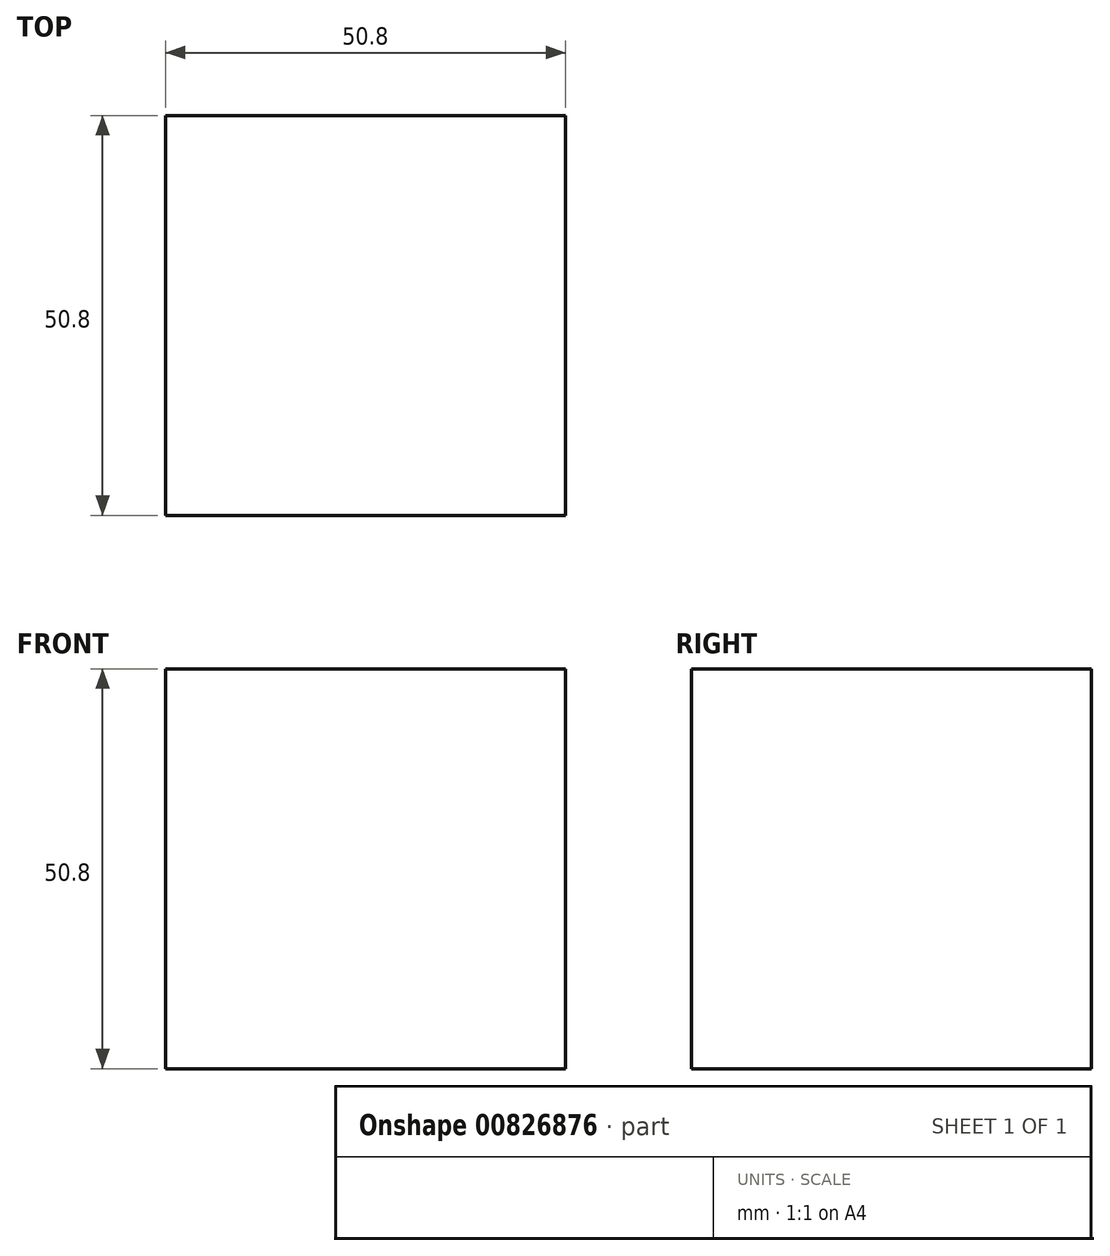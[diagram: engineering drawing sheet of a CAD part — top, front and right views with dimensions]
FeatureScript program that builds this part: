
annotation { "Feature Type Name" : "Feature", "Feature Type Description" : "" }
export const myFeature = defineFeature(function(context is Context, id is Id, definition is map)
    precondition{}
    {
        {
            var Q0;
            Q0=qCreatedBy(makeId("Top.planeOp"),FACE);
            var sketch = newSketch(context, id + "F0", { "sketchPlane" : qUnion([Q0])});
            skLineSegment(sketch, "E0.bottom", {"start": v(-25.4, 25.4) * mm, "end": v(25.4, 25.4) * mm});
            skLineSegment(sketch, "E0.top", {"start": v(-25.4, -25.4) * mm, "end": v(25.4, -25.4) * mm});
            skLineSegment(sketch, "E0.left", {"start": v(-25.4, 25.4) * mm, "end": v(-25.4, -25.4) * mm});
            skLineSegment(sketch, "E0.right", {"start": v(25.4, 25.4) * mm, "end": v(25.4, -25.4) * mm});
            skSolve(sketch);
        }
        {
            var Q0;
            Q0=makeQuery(id+"F0.imprint","IMPRINT",FACE,{"disambiguationData":[TD([[makeQuery(id+"F0.imprint","IMPRINT",EDGE,{"derivedFrom":sQuery(id+"F0.wireOp",EDGE,"E0.bottom")}),-1.0]])]});
            extrude(context, id + "F1", {"entities" : qUnion([Q0]), "depth" : 50.8 * mm, "offsetDistance" : 25.4 * mm});
        }
    });
